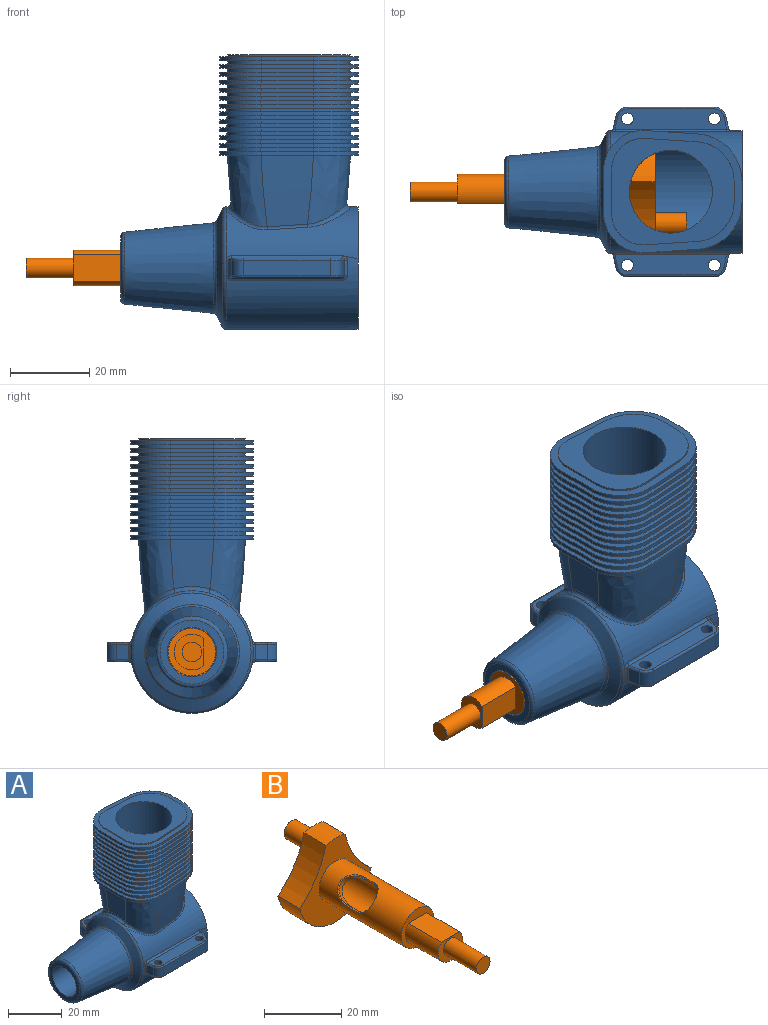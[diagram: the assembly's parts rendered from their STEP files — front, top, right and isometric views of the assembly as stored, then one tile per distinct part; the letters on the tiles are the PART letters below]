
ASSEMBLY  parts=2 mates=1
PART A: 325 faces, bbox 60.4x43.8x74.2 mm
  f0: cylinder r=14mm len=30mm, axis (1,0,0), area 2236mm2, adj f1,f239,f252,f317,f318,f321,f322,f323
  f1: cylinder r=10.5mm len=44.1mm, axis (0,0,1), area 2779.1mm2, adj f0,f20,f317,f318,f319,f320,f321,f322
  f2: bspline ~45.01x32.7mm, area 13.2mm2, adj f7,f9,f18,f56
  f3: bspline ~45.01x29.7mm, area 11mm2, adj f6,f7,f18,f56
  f4: bspline ~45.01x32.7mm, area 13.2mm2, adj f6,f8,f18,f56
  f5: bspline ~45.01x25.49mm, area 5.3mm2, adj f8,f9,f18,f56
  f6: bspline ~8.6x8.58mm, area 13mm2, adj f3,f4,f18,f56
  f7: bspline ~8.6x8.58mm, area 13mm2, adj f2,f3,f18,f56
  f8: bspline ~10.03x9.41mm, area 15mm2, adj f4,f5,f18,f56
  f9: bspline ~10.03x9.41mm, area 15mm2, adj f2,f5,f18,f56
  f10: plane 13.13x1mm, normal (0.06,-1,0), area 13.2mm2, adj f11,f17,f18,f19
  f11: cylinder r=12mm len=11.98mm, axis (0,0,1), area 18.1mm2, adj f10,f12,f18,f19
  f12: plane 5.25x1mm, normal (1,0,0), area 5.2mm2, adj f11,f13,f18,f19
  f13: cylinder r=12mm len=11.98mm, axis (0,0,1), area 18.1mm2, adj f12,f14,f18,f19
  f14: plane 13.13x1mm, normal (0.06,1,0), area 13.2mm2, adj f13,f15,f18,f19
  f15: cylinder r=10mm len=10.64mm, axis (0,0,1), area 16.4mm2, adj f14,f16,f18,f19
  f16: plane 10.93x1mm, normal (-1,0,0), area 10.9mm2, adj f15,f17,f18,f19
  f17: cylinder r=10mm len=10.64mm, axis (0,0,1), area 16.4mm2, adj f10,f16,f18,f19
  f18: plane 35.31x31.24mm, normal (0,0,-1), area 208.1mm2, adj f2,f3,f4,f5,f6,f7,f8,f9
  f19: plane 35.31x31.24mm, normal (0,0,1), area 209mm2, adj f10,f11,f12,f13,f14,f15,f16,f17
  f20: plane 31.29x27.22mm, normal (0,0,1), area 390.9mm2, adj f1,f21,f22,f23,f24,f25,f26,f27
  f21: bspline ~9.98x9.36mm, area 7.5mm2, adj f20,f22,f28,f29
  f22: bspline ~45.01x25.49mm, area 2.6mm2, adj f20,f21,f23,f29
  f23: bspline ~9.98x9.36mm, area 7.5mm2, adj f20,f22,f24,f29
  f24: bspline ~45.01x32.7mm, area 6.6mm2, adj f20,f23,f25,f29
  f25: bspline ~8.54x8.52mm, area 6.5mm2, adj f20,f24,f26,f29
  f26: bspline ~45.01x29.7mm, area 5.5mm2, adj f20,f25,f27,f29
  f27: bspline ~8.54x8.52mm, area 6.5mm2, adj f20,f26,f28,f29
  f28: bspline ~45.01x32.7mm, area 6.6mm2, adj f20,f21,f27,f29
  f29: plane 35.3x31.24mm, normal (0,0,1), area 210.1mm2, adj f21,f22,f23,f24,f25,f26,f27,f28
  f30: cylinder r=12mm len=11.98mm, axis (0,0,1), area 18.1mm2, adj f29,f31,f37,f38
  f31: plane 5.25x1mm, normal (1,0,0), area 5.2mm2, adj f29,f30,f32,f38
  f32: cylinder r=12mm len=11.98mm, axis (0,0,1), area 18.1mm2, adj f29,f31,f33,f38
  f33: plane 13.13x1mm, normal (0.06,1,0), area 13.2mm2, adj f29,f32,f34,f38
  f34: cylinder r=10mm len=10.64mm, axis (0,0,1), area 16.4mm2, adj f29,f33,f35,f38
  f35: plane 10.93x1mm, normal (-1,0,0), area 10.9mm2, adj f29,f34,f36,f38
  f36: cylinder r=10mm len=10.64mm, axis (0,0,1), area 16.4mm2, adj f29,f35,f37,f38
  f37: plane 13.13x1mm, normal (0.06,-1,0), area 13.2mm2, adj f29,f30,f36,f38
  f38: plane 35.31x31.24mm, normal (0,0,-1), area 209.7mm2, adj f30,f31,f32,f33,f34,f35,f36,f37
  f39: bspline ~8.55x8.54mm, area 13mm2, adj f19,f38,f45,f46
  f40: bspline ~8.55x8.54mm, area 13mm2, adj f19,f38,f44,f45
  f41: bspline ~9.99x9.37mm, area 15mm2, adj f19,f38,f43,f44
  f42: bspline ~9.99x9.37mm, area 15mm2, adj f19,f38,f43,f46
  f43: bspline ~45.01x25.49mm, area 5.3mm2, adj f19,f38,f41,f42
  f44: bspline ~45.01x32.7mm, area 13.2mm2, adj f19,f38,f40,f41
  f45: bspline ~45.01x29.7mm, area 10.9mm2, adj f19,f38,f39,f40
  f46: bspline ~45.01x32.7mm, area 13.2mm2, adj f19,f38,f39,f42
  f47: plane 13.13x1mm, normal (0.06,-1,0), area 13.2mm2, adj f48,f54,f55,f56
  f48: cylinder r=12mm len=11.98mm, axis (0,0,1), area 18.1mm2, adj f47,f49,f55,f56
  f49: plane 5.25x1mm, normal (1,0,0), area 5.2mm2, adj f48,f50,f55,f56
  f50: cylinder r=12mm len=11.98mm, axis (0,0,1), area 18.1mm2, adj f49,f51,f55,f56
  f51: plane 13.13x1mm, normal (0.06,1,0), area 13.2mm2, adj f50,f52,f55,f56
  f52: cylinder r=10mm len=10.64mm, axis (0,0,1), area 16.4mm2, adj f51,f53,f55,f56
  f53: plane 10.93x1mm, normal (-1,0,0), area 10.9mm2, adj f52,f54,f55,f56
  f54: cylinder r=10mm len=10.64mm, axis (0,0,1), area 16.4mm2, adj f47,f53,f55,f56
  f55: plane 35.31x31.25mm, normal (0,0,-1), area 205.5mm2, adj f47,f48,f49,f50,f51,f52,f53,f54
  f56: plane 35.31x31.24mm, normal (0,0,1), area 206.9mm2, adj f2,f3,f4,f5,f6,f7,f8,f9
  f57: bspline ~8.6x8.58mm, area 13mm2, adj f55,f63,f64,f74
  f58: bspline ~8.6x8.58mm, area 13mm2, adj f55,f62,f63,f74
  f59: bspline ~10.06x9.45mm, area 15mm2, adj f55,f61,f62,f74
  f60: bspline ~10.06x9.45mm, area 15mm2, adj f55,f61,f64,f74
  f61: bspline ~45.01x25.49mm, area 5.3mm2, adj f55,f59,f60,f74
  f62: bspline ~45.01x32.7mm, area 13.3mm2, adj f55,f58,f59,f74
  f63: bspline ~45.01x29.7mm, area 11mm2, adj f55,f57,f58,f74
  f64: bspline ~45.01x32.7mm, area 13.3mm2, adj f55,f57,f60,f74
  f65: plane 13.13x1mm, normal (0.06,-1,0), area 13.2mm2, adj f66,f72,f73,f74
  f66: cylinder r=12mm len=11.98mm, axis (0,0,1), area 18.1mm2, adj f65,f67,f73,f74
  f67: plane 5.25x1mm, normal (1,0,0), area 5.2mm2, adj f66,f68,f73,f74
  f68: cylinder r=12mm len=11.98mm, axis (0,0,1), area 18.1mm2, adj f67,f69,f73,f74
  f69: plane 13.13x1mm, normal (0.06,1,0), area 13.2mm2, adj f68,f70,f73,f74
  f70: cylinder r=10mm len=10.64mm, axis (0,0,1), area 16.4mm2, adj f69,f71,f73,f74
  f71: plane 10.93x1mm, normal (-1,0,0), area 10.9mm2, adj f70,f72,f73,f74
  f72: cylinder r=10mm len=10.64mm, axis (0,0,1), area 16.4mm2, adj f65,f71,f73,f74
  f73: plane 35.31x31.25mm, normal (0,0,-1), area 202.3mm2, adj f65,f66,f67,f68,f69,f70,f71,f72
  f74: plane 35.31x31.25mm, normal (0,0,1), area 203.9mm2, adj f57,f58,f59,f60,f61,f62,f63,f64
  f75: bspline ~45.01x29.7mm, area 11.1mm2, adj f73,f81,f82,f92
  f76: bspline ~45.01x32.7mm, area 13.3mm2, adj f73,f80,f81,f92
  f77: bspline ~45.01x25.49mm, area 5.4mm2, adj f73,f79,f80,f92
  f78: bspline ~45.01x32.7mm, area 13.3mm2, adj f73,f79,f82,f92
  f79: bspline ~10.04x9.43mm, area 15.1mm2, adj f73,f77,f78,f92
  f80: bspline ~10.04x9.43mm, area 15.1mm2, adj f73,f76,f77,f92
  f81: bspline ~8.63x8.61mm, area 13.1mm2, adj f73,f75,f76,f92
  f82: bspline ~8.63x8.61mm, area 13.1mm2, adj f73,f75,f78,f92
  f83: plane 13.13x1mm, normal (0.06,-1,0), area 13.2mm2, adj f84,f90,f91,f92
  f84: cylinder r=12mm len=11.98mm, axis (0,0,1), area 18.1mm2, adj f83,f85,f91,f92
  f85: plane 5.25x1mm, normal (1,0,0), area 5.2mm2, adj f84,f86,f91,f92
  f86: cylinder r=12mm len=11.98mm, axis (0,0,1), area 18.1mm2, adj f85,f87,f91,f92
  f87: plane 13.13x1mm, normal (0.06,1,0), area 13.2mm2, adj f86,f88,f91,f92
  f88: cylinder r=10mm len=10.64mm, axis (0,0,1), area 16.4mm2, adj f87,f89,f91,f92
  f89: plane 10.93x1mm, normal (-1,0,0), area 10.9mm2, adj f88,f90,f91,f92
  f90: cylinder r=10mm len=10.64mm, axis (0,0,1), area 16.4mm2, adj f83,f89,f91,f92
  f91: plane 35.31x31.25mm, normal (0,0,-1), area 198.8mm2, adj f83,f84,f85,f86,f87,f88,f89,f90
  f92: plane 35.31x31.25mm, normal (0,0,1), area 200.6mm2, adj f75,f76,f77,f78,f79,f80,f81,f82
  f93: bspline ~8.63x8.61mm, area 13.1mm2, adj f91,f99,f100,f110
  f94: bspline ~10.05x9.44mm, area 15.1mm2, adj f91,f98,f99,f110
  f95: bspline ~10.05x9.44mm, area 15.1mm2, adj f91,f97,f98,f110
  f96: bspline ~8.63x8.61mm, area 13.1mm2, adj f91,f97,f100,f110
  f97: bspline ~45.01x32.7mm, area 13.4mm2, adj f91,f95,f96,f110
  f98: bspline ~45.01x25.49mm, area 5.4mm2, adj f91,f94,f95,f110
  f99: bspline ~45.01x32.7mm, area 13.4mm2, adj f91,f93,f94,f110
  f100: bspline ~45.01x29.7mm, area 11.2mm2, adj f91,f93,f96,f110
  f101: plane 13.13x1mm, normal (0.06,-1,0), area 13.2mm2, adj f102,f108,f109,f110
  f102: cylinder r=12mm len=11.98mm, axis (0,0,1), area 18.1mm2, adj f101,f103,f109,f110
  f103: plane 5.25x1mm, normal (1,0,0), area 5.2mm2, adj f102,f104,f109,f110
  f104: cylinder r=12mm len=11.98mm, axis (0,0,1), area 18.1mm2, adj f103,f105,f109,f110
  f105: plane 13.13x1mm, normal (0.06,1,0), area 13.2mm2, adj f104,f106,f109,f110
  f106: cylinder r=10mm len=10.64mm, axis (0,0,1), area 16.4mm2, adj f105,f107,f109,f110
  f107: plane 10.93x1mm, normal (-1,0,0), area 10.9mm2, adj f106,f108,f109,f110
  f108: cylinder r=10mm len=10.64mm, axis (0,0,1), area 16.4mm2, adj f101,f107,f109,f110
  f109: plane 35.31x31.25mm, normal (0,0,-1), area 195.4mm2, adj f101,f102,f103,f104,f105,f106,f107,f108
  f110: plane 35.31x31.25mm, normal (0,0,1), area 197.1mm2, adj f93,f94,f95,f96,f97,f98,f99,f100
  f111: bspline ~45.01x32.7mm, area 13.4mm2, adj f109,f117,f118,f128
  f112: bspline ~45.01x25.49mm, area 5.5mm2, adj f109,f116,f117,f128
  f113: bspline ~45.01x32.7mm, area 13.4mm2, adj f109,f115,f116,f128
  f114: bspline ~45.01x29.7mm, area 11.2mm2, adj f109,f115,f118,f128
  f115: bspline ~8.62x8.6mm, area 13.1mm2, adj f109,f113,f114,f128
  f116: bspline ~10.05x9.44mm, area 15.1mm2, adj f109,f112,f113,f128
  f117: bspline ~10.05x9.44mm, area 15.1mm2, adj f109,f111,f112,f128
  f118: bspline ~8.62x8.6mm, area 13.1mm2, adj f109,f111,f114,f128
  f119: plane 13.13x1mm, normal (0.06,-1,0), area 13.2mm2, adj f120,f126,f127,f128
  f120: cylinder r=12mm len=11.98mm, axis (0,0,1), area 18.1mm2, adj f119,f121,f127,f128
  f121: plane 5.25x1mm, normal (1,0,0), area 5.2mm2, adj f120,f122,f127,f128
  f122: cylinder r=12mm len=11.98mm, axis (0,0,1), area 18.1mm2, adj f121,f123,f127,f128
  f123: plane 13.13x1mm, normal (0.06,1,0), area 13.2mm2, adj f122,f124,f127,f128
  f124: cylinder r=10mm len=10.64mm, axis (0,0,1), area 16.4mm2, adj f123,f125,f127,f128
  f125: plane 10.93x1mm, normal (-1,0,0), area 10.9mm2, adj f124,f126,f127,f128
  f126: cylinder r=10mm len=10.64mm, axis (0,0,1), area 16.4mm2, adj f119,f125,f127,f128
  f127: plane 35.31x31.24mm, normal (0,0,-1), area 192.5mm2, adj f119,f120,f121,f122,f123,f124,f125,f126
  f128: plane 35.31x31.25mm, normal (0,0,1), area 193.9mm2, adj f111,f112,f113,f114,f115,f116,f117,f118
  f129: bspline ~10.03x9.41mm, area 15.1mm2, adj f127,f135,f136,f146
  f130: bspline ~10.03x9.41mm, area 15.1mm2, adj f127,f134,f135,f146
  f131: bspline ~10.73x8.62mm, area 13.1mm2, adj f127,f133,f134,f146
  f132: bspline ~10.73x8.62mm, area 13.1mm2, adj f127,f133,f136,f146
  f133: bspline ~45.01x29.7mm, area 11.3mm2, adj f127,f131,f132,f146
  f134: bspline ~45.01x32.7mm, area 13.5mm2, adj f127,f130,f131,f146
  f135: bspline ~45.01x25.49mm, area 5.5mm2, adj f127,f129,f130,f146
  f136: bspline ~45.01x32.7mm, area 13.5mm2, adj f127,f129,f132,f146
  f137: plane 13.13x1mm, normal (0.06,-1,0), area 13.2mm2, adj f138,f144,f145,f146
  f138: cylinder r=12mm len=11.98mm, axis (0,0,1), area 18.1mm2, adj f137,f139,f145,f146
  f139: plane 5.25x1mm, normal (1,0,0), area 5.2mm2, adj f138,f140,f145,f146
  f140: cylinder r=12mm len=11.98mm, axis (0,0,1), area 18.1mm2, adj f139,f141,f145,f146
  f141: plane 13.13x1mm, normal (0.06,1,0), area 13.2mm2, adj f140,f142,f145,f146
  f142: cylinder r=10mm len=10.64mm, axis (0,0,1), area 16.4mm2, adj f141,f143,f145,f146
  f143: plane 10.93x1mm, normal (-1,0,0), area 10.9mm2, adj f142,f144,f145,f146
  f144: cylinder r=10mm len=10.64mm, axis (0,0,1), area 16.4mm2, adj f137,f143,f145,f146
  f145: plane 35.31x31.24mm, normal (0,0,-1), area 190.3mm2, adj f137,f138,f139,f140,f141,f142,f143,f144
  f146: plane 35.31x31.24mm, normal (0,0,1), area 191.3mm2, adj f129,f130,f131,f132,f133,f134,f135,f136
  f147: bspline ~45.01x25.49mm, area 5.6mm2, adj f145,f153,f154,f164
  f148: bspline ~45.01x32.7mm, area 13.5mm2, adj f145,f152,f153,f164
  f149: bspline ~45.01x29.7mm, area 11.3mm2, adj f145,f151,f152,f164
  f150: bspline ~45.01x32.7mm, area 13.5mm2, adj f145,f151,f154,f164
  f151: bspline ~8.57x8.55mm, area 13.2mm2, adj f145,f149,f150,f164
  f152: bspline ~8.57x8.55mm, area 13.2mm2, adj f145,f148,f149,f164
  f153: bspline ~10.03x9.44mm, area 15.2mm2, adj f145,f147,f148,f164
  f154: bspline ~10.03x9.44mm, area 15.2mm2, adj f145,f147,f150,f164
  f155: plane 13.13x1mm, normal (0.06,-1,0), area 13.2mm2, adj f156,f162,f163,f164
  f156: cylinder r=12mm len=11.98mm, axis (0,0,1), area 18.1mm2, adj f155,f157,f163,f164
  f157: plane 5.25x1mm, normal (1,0,0), area 5.2mm2, adj f156,f158,f163,f164
  f158: cylinder r=12mm len=11.98mm, axis (0,0,1), area 18.1mm2, adj f157,f159,f163,f164
  f159: plane 13.13x1mm, normal (0.06,1,0), area 13.2mm2, adj f158,f160,f163,f164
  f160: cylinder r=10mm len=10.64mm, axis (0,0,1), area 16.4mm2, adj f159,f161,f163,f164
  f161: plane 10.93x1mm, normal (-1,0,0), area 10.9mm2, adj f160,f162,f163,f164
  f162: cylinder r=10mm len=10.64mm, axis (0,0,1), area 16.4mm2, adj f155,f161,f163,f164
  f163: plane 35.3x31.24mm, normal (0,0,-1), area 189.2mm2, adj f155,f156,f157,f158,f159,f160,f161,f162
  f164: plane 35.31x31.24mm, normal (0,0,1), area 189.6mm2, adj f147,f148,f149,f150,f151,f152,f153,f154
  f165: bspline ~9.99x9.37mm, area 15.2mm2, adj f163,f171,f172,f182
  f166: bspline ~11.01x8.6mm, area 13.2mm2, adj f163,f170,f171,f182
  f167: bspline ~11.01x8.6mm, area 13.2mm2, adj f163,f169,f170,f182
  f168: bspline ~9.99x9.37mm, area 15.2mm2, adj f163,f169,f172,f182
  f169: bspline ~45.01x32.7mm, area 13.5mm2, adj f163,f167,f168,f182
  f170: bspline ~45.01x29.7mm, area 11.3mm2, adj f163,f166,f167,f182
  f171: bspline ~45.01x32.7mm, area 13.5mm2, adj f163,f165,f166,f182
  f172: bspline ~45.01x25.49mm, area 5.6mm2, adj f163,f165,f168,f182
  f173: plane 13.13x1mm, normal (0.06,-1,0), area 13.2mm2, adj f174,f180,f181,f182
  f174: cylinder r=12mm len=11.98mm, axis (0,0,1), area 18.1mm2, adj f173,f175,f181,f182
  f175: plane 5.25x1mm, normal (1,0,0), area 5.2mm2, adj f174,f176,f181,f182
  f176: cylinder r=12mm len=11.98mm, axis (0,0,1), area 18.1mm2, adj f175,f177,f181,f182
  f177: plane 13.13x1mm, normal (0.06,1,0), area 13.2mm2, adj f176,f178,f181,f182
  f178: cylinder r=10mm len=10.64mm, axis (0,0,1), area 16.4mm2, adj f177,f179,f181,f182
  f179: plane 10.93x1mm, normal (-1,0,0), area 10.9mm2, adj f178,f180,f181,f182
  f180: cylinder r=10mm len=10.64mm, axis (0,0,1), area 16.4mm2, adj f173,f179,f181,f182
  f181: plane 35.31x31.24mm, normal (0,0,-1), area 189.6mm2, adj f173,f174,f175,f176,f177,f178,f179,f180
  f182: plane 35.3x31.24mm, normal (0,0,1), area 189.2mm2, adj f165,f166,f167,f168,f169,f170,f171,f172
  f183: bspline ~45.01x32.7mm, area 13.5mm2, adj f181,f189,f190,f200
  f184: bspline ~45.01x29.7mm, area 11.3mm2, adj f181,f188,f189,f200
  f185: bspline ~45.01x32.7mm, area 13.5mm2, adj f181,f187,f188,f200
  f186: bspline ~45.01x25.49mm, area 5.6mm2, adj f181,f187,f190,f200
  f187: bspline ~10.05x9.43mm, area 15.2mm2, adj f181,f185,f186,f200
  f188: bspline ~8.6x8.58mm, area 13.2mm2, adj f181,f184,f185,f200
  f189: bspline ~8.6x8.58mm, area 13.2mm2, adj f181,f183,f184,f200
  f190: bspline ~10.05x9.43mm, area 15.2mm2, adj f181,f183,f186,f200
  f191: plane 13.13x1mm, normal (0.06,-1,0), area 13.2mm2, adj f192,f198,f199,f200
  f192: cylinder r=12mm len=11.98mm, axis (0,0,1), area 18.1mm2, adj f191,f193,f199,f200
  f193: plane 5.25x1mm, normal (1,0,0), area 5.2mm2, adj f192,f194,f199,f200
  f194: cylinder r=12mm len=11.98mm, axis (0,0,1), area 18.1mm2, adj f193,f195,f199,f200
  f195: plane 13.13x1mm, normal (0.06,1,0), area 13.2mm2, adj f194,f196,f199,f200
  f196: cylinder r=10mm len=10.64mm, axis (0,0,1), area 16.4mm2, adj f195,f197,f199,f200
  f197: plane 10.93x1mm, normal (-1,0,0), area 10.9mm2, adj f196,f198,f199,f200
  f198: cylinder r=10mm len=10.64mm, axis (0,0,1), area 16.4mm2, adj f191,f197,f199,f200
  f199: plane 35.31x31.25mm, normal (0,0,-1), area 191.8mm2, adj f191,f192,f193,f194,f195,f196,f197,f198
  f200: plane 35.31x31.24mm, normal (0,0,1), area 190.5mm2, adj f183,f184,f185,f186,f187,f188,f189,f190
  f201: bspline ~12.75x8.81mm, area 13.2mm2, adj f199,f207,f208,f218
  f202: bspline ~12.75x8.81mm, area 13.2mm2, adj f199,f206,f207,f218
  f203: bspline ~10.05x9.43mm, area 15.2mm2, adj f199,f205,f206,f218
  f204: bspline ~10.05x9.43mm, area 15.2mm2, adj f199,f205,f208,f218
  f205: bspline ~45.01x25.49mm, area 5.5mm2, adj f199,f203,f204,f218
  f206: bspline ~45.01x32.7mm, area 13.5mm2, adj f199,f202,f203,f218
  f207: bspline ~45.01x29.7mm, area 11.3mm2, adj f199,f201,f202,f218
  f208: bspline ~45.01x32.7mm, area 13.5mm2, adj f199,f201,f204,f218
  f209: plane 13.13x1mm, normal (0.06,-1,0), area 13.2mm2, adj f210,f216,f217,f218
  f210: cylinder r=12mm len=11.98mm, axis (0,0,1), area 18.1mm2, adj f209,f211,f217,f218
  f211: plane 5.25x1mm, normal (1,0,0), area 5.2mm2, adj f210,f212,f217,f218
  f212: cylinder r=12mm len=11.98mm, axis (0,0,1), area 18.1mm2, adj f211,f213,f217,f218
  f213: plane 13.13x1mm, normal (0.06,1,0), area 13.2mm2, adj f212,f214,f217,f218
  f214: cylinder r=10mm len=10.64mm, axis (0,0,1), area 16.4mm2, adj f213,f215,f217,f218
  f215: plane 10.93x1mm, normal (-1,0,0), area 10.9mm2, adj f214,f216,f217,f218
  f216: cylinder r=10mm len=10.64mm, axis (0,0,1), area 16.4mm2, adj f209,f215,f217,f218
  f217: plane 35.33x31.26mm, normal (0,0,-1), area 196.2mm2, adj f209,f210,f211,f212,f213,f214,f215,f216
  f218: plane 35.32x31.25mm, normal (0,0,1), area 193.7mm2, adj f201,f202,f203,f204,f205,f206,f207,f208
  f219: bspline ~45.01x29.7mm, area 11.2mm2, adj f217,f225,f226,f236
  f220: bspline ~45.01x32.7mm, area 13.4mm2, adj f217,f224,f225,f236
  f221: bspline ~45.01x25.49mm, area 5.5mm2, adj f217,f223,f224,f236
  f222: bspline ~45.01x32.7mm, area 13.4mm2, adj f217,f223,f226,f236
  f223: bspline ~10.16x9.57mm, area 15.3mm2, adj f217,f221,f222,f236
  f224: bspline ~10.16x9.57mm, area 15.3mm2, adj f217,f220,f221,f236
  f225: bspline ~8.79x8.78mm, area 13.3mm2, adj f217,f219,f220,f236
  f226: bspline ~8.79x8.78mm, area 13.3mm2, adj f217,f219,f222,f236
  f227: plane 13.13x1mm, normal (0.06,-1,0), area 13.2mm2, adj f228,f234,f235,f236
  f228: cylinder r=12mm len=11.98mm, axis (0,0,1), area 18.1mm2, adj f227,f229,f235,f236
  f229: plane 5.25x1mm, normal (1,0,0), area 5.2mm2, adj f228,f230,f235,f236
  f230: cylinder r=12mm len=11.98mm, axis (0,0,1), area 18.1mm2, adj f229,f231,f235,f236
  f231: plane 13.13x1mm, normal (0.06,1,0), area 13.2mm2, adj f230,f232,f235,f236
  f232: cylinder r=10mm len=10.64mm, axis (0,0,1), area 16.4mm2, adj f231,f233,f235,f236
  f233: plane 10.93x1mm, normal (-1,0,0), area 10.9mm2, adj f232,f234,f235,f236
  f234: cylinder r=10mm len=10.64mm, axis (0,0,1), area 16.4mm2, adj f227,f233,f235,f236
  f235: plane 35.35x31.29mm, normal (0,0,-1), area 203mm2, adj f227,f228,f229,f230,f231,f232,f233,f234
  f236: plane 35.34x31.27mm, normal (0,0,1), area 199.3mm2, adj f219,f220,f221,f222,f223,f224,f225,f226
  f237: cylinder r=6.25mm len=30mm, axis (-1,0,0), area 1178.1mm2, adj f238,f239
  f238: plane 16.2x16.2mm, normal (-1,0,0), area 83.4mm2, adj f237,f316
  f239: plane 28x28mm, normal (1,0,0), area 493mm2, adj f0,f237
  f240: cone r=9mm half-angle=6deg, axis (1,0,0), area 1465.2mm2, adj f315,f316
  f241: cylinder r=3mm len=4mm, axis (0,0,-1), area 16.3mm2, adj f242,f254,f273,f283
  f242: plane 22x4mm, normal (0,1,0), area 88mm2, adj f241,f245,f272,f282
  f243: cylinder r=1.5mm len=5mm, axis (0,0,1), area 47.1mm2, adj f253,f255
  f244: cylinder r=1.5mm len=5mm, axis (0,0,1), area 47.1mm2, adj f253,f255
  f245: cylinder r=3mm len=4mm, axis (0,0,-1), area 16.3mm2, adj f242,f256,f271,f281
  f246: cylinder r=3mm len=4mm, axis (0,0,-1), area 16.3mm2, adj f247,f258,f276,f286
  f247: plane 22x4mm, normal (0,-1,0), area 88mm2, adj f246,f250,f277,f287
  f248: cylinder r=1.5mm len=5mm, axis (0,0,1), area 47.1mm2, adj f257,f259
  f249: cylinder r=1.5mm len=5mm, axis (0,0,1), area 47.1mm2, adj f257,f259
  f250: cylinder r=3mm len=4mm, axis (0,0,-1), area 16.3mm2, adj f247,f260,f278,f288
  f251: cone r=11.52mm half-angle=63.3deg, axis (1,0,0), area 278.6mm2, adj f314,f315
  f252: plane 31x31mm, normal (1,0,0), area 139mm2, adj f0,f261
  f253: plane 28.21x5.08mm, normal (0,0,-1), area 122mm2, adj f243,f244,f270,f271,f272,f273,f274,f305
  f254: plane 4x3.15mm, normal (-0.98,0.21,0), area 12.6mm2, adj f241,f274,f284,f302
  f255: plane 28.21x5.08mm, normal (0,0,1), area 122mm2, adj f243,f244,f280,f281,f282,f283,f284,f298
  f256: plane 4x3.15mm, normal (0.98,0.21,0), area 12.6mm2, adj f245,f270,f280,f301
  f257: plane 28.21x5.08mm, normal (0,0,-1), area 122mm2, adj f248,f249,f275,f276,f277,f278,f279,f297
  f258: plane 4x3.15mm, normal (0.98,-0.21,0), area 12.6mm2, adj f246,f275,f285,f294
  f259: plane 28.21x5.08mm, normal (0,0,1), area 122mm2, adj f248,f249,f285,f286,f287,f288,f289,f290
  f260: plane 4x3.15mm, normal (-0.98,-0.21,0), area 12.6mm2, adj f250,f279,f289,f293
  f261: cylinder r=15.5mm len=33.38mm, axis (1,0,0), area 2139.1mm2, adj f252,f290,f291,f292,f293,f294,f295,f296
  f262: bspline ~27.82x10.76mm, area 203.5mm2, adj f235,f268,f269,f306
  f263: bspline ~27.67x11.96mm, area 224.8mm2, adj f235,f267,f268,f310
  f264: bspline ~27.67x11.96mm, area 224.8mm2, adj f235,f266,f267,f313
  f265: bspline ~27.82x10.76mm, area 203.5mm2, adj f235,f266,f269,f309
  f266: bspline ~54x32.7mm, area 210.8mm2, adj f235,f264,f265,f311
  f267: bspline ~54x25.49mm, area 55.9mm2, adj f235,f263,f264,f312
  f268: bspline ~54x32.7mm, area 210.8mm2, adj f235,f262,f263,f308
  f269: bspline ~54x29.7mm, area 128.4mm2, adj f235,f262,f265,f307
  f270: cylinder r=0.5mm len=3.26mm, axis (-0.21,0.98,0), area 2.5mm2, adj f253,f256,f271,f303
  f271: torus R=2.5mm, axis (0,0,1), area 3mm2, adj f245,f253,f270,f272
  f272: cylinder r=0.5mm len=22mm, axis (-1,0,0), area 17.3mm2, adj f242,f253,f271,f273
  f273: torus R=2.5mm, axis (0,0,1), area 3mm2, adj f241,f253,f272,f274
  f274: cylinder r=0.5mm len=3.26mm, axis (-0.21,-0.98,0), area 2.5mm2, adj f253,f254,f273,f304
  f275: cylinder r=0.5mm len=3.26mm, axis (0.21,0.98,0), area 2.5mm2, adj f257,f258,f276,f296
  f276: torus R=2.5mm, axis (0,0,1), area 3mm2, adj f246,f257,f275,f277
  f277: cylinder r=0.5mm len=22mm, axis (1,0,0), area 17.3mm2, adj f247,f257,f276,f278
  f278: torus R=2.5mm, axis (0,0,1), area 3mm2, adj f250,f257,f277,f279
  f279: cylinder r=0.5mm len=3.26mm, axis (0.21,-0.98,0), area 2.5mm2, adj f257,f260,f278,f295
  f280: cylinder r=0.5mm len=3.26mm, axis (0.21,-0.98,0), area 2.5mm2, adj f255,f256,f281,f299
  f281: torus R=2.5mm, axis (0,0,1), area 3mm2, adj f245,f255,f280,f282
  f282: cylinder r=0.5mm len=22mm, axis (1,0,0), area 17.3mm2, adj f242,f255,f281,f283
  f283: torus R=2.5mm, axis (0,0,1), area 3mm2, adj f241,f255,f282,f284
  f284: cylinder r=0.5mm len=3.26mm, axis (0.21,0.98,0), area 2.5mm2, adj f254,f255,f283,f300
  f285: cylinder r=0.5mm len=3.26mm, axis (-0.21,-0.98,0), area 2.5mm2, adj f258,f259,f286,f292
  f286: torus R=2.5mm, axis (0,0,1), area 3mm2, adj f246,f259,f285,f287
  f287: cylinder r=0.5mm len=22mm, axis (-1,0,0), area 17.3mm2, adj f247,f259,f286,f288
  f288: torus R=2.5mm, axis (0,0,1), area 3mm2, adj f250,f259,f287,f289
  f289: cylinder r=0.5mm len=3.26mm, axis (-0.21,0.98,0), area 2.5mm2, adj f259,f260,f288,f291
  f290: cylinder r=0.75mm len=28.21mm, axis (1,0,0), area 29mm2, adj f259,f261,f291,f292
  f291: bspline ~1.53x1.46mm, area 1.2mm2, adj f261,f289,f290,f293
  f292: bspline ~1.53x1.46mm, area 1.2mm2, adj f261,f285,f290,f294
  f293: bspline ~4x0.76mm, area 4mm2, adj f260,f261,f291,f295
  f294: bspline ~4x0.76mm, area 4mm2, adj f258,f261,f292,f296
  f295: bspline ~1.53x1.46mm, area 1.2mm2, adj f261,f279,f293,f297
  f296: bspline ~1.53x1.46mm, area 1.2mm2, adj f261,f275,f294,f297
  f297: cylinder r=0.75mm len=28.21mm, axis (1,0,0), area 29mm2, adj f257,f261,f295,f296
  f298: cylinder r=0.75mm len=28.21mm, axis (1,0,0), area 29mm2, adj f255,f261,f299,f300
  f299: bspline ~1.53x1.46mm, area 1.2mm2, adj f261,f280,f298,f301
  f300: bspline ~1.53x1.46mm, area 1.2mm2, adj f261,f284,f298,f302
  f301: bspline ~4x0.76mm, area 4mm2, adj f256,f261,f299,f303
  f302: bspline ~4x0.76mm, area 4mm2, adj f254,f261,f300,f304
  f303: bspline ~1.53x1.46mm, area 1.2mm2, adj f261,f270,f301,f305
  f304: bspline ~1.53x1.46mm, area 1.2mm2, adj f261,f274,f302,f305
  f305: cylinder r=0.75mm len=28.21mm, axis (1,0,0), area 29mm2, adj f253,f261,f303,f304
  f306: bspline ~11.84x9.37mm, area 17.8mm2, adj f261,f262,f307,f308
  f307: bspline ~12.74x2.31mm, area 15.1mm2, adj f261,f269,f306,f309
  f308: bspline ~21.25x2.14mm, area 8.4mm2, adj f261,f268,f306,f310
  f309: bspline ~10.62x9.37mm, area 17.8mm2, adj f261,f265,f307,f311
  f310: bspline ~11.73x11.38mm, area 21mm2, adj f261,f263,f308,f312
  f311: bspline ~21.25x2.14mm, area 8.4mm2, adj f261,f266,f309,f313
  f312: bspline ~7.54x1.51mm, area 6.3mm2, adj f261,f267,f310,f313
  f313: bspline ~12.84x11.73mm, area 21mm2, adj f261,f264,f311,f312
  f314: torus R=14.5mm, axis (-1,0,0), area 106.3mm2, adj f251,f261
  f315: torus R=12.46mm, axis (1,0,0), area 73.3mm2, adj f240,f251
  f316: torus R=8.1mm, axis (1,0,0), area 80.2mm2, adj f238,f240
  f317: plane 3.69x1.52mm, normal (-1,0,0), area 1.2mm2, adj f0,f1,f319,f323
  f318: plane 3.69x1.52mm, normal (1,0,0), area 1.2mm2, adj f0,f1,f319,f323
  f319: cylinder r=11mm len=7mm, axis (1,0,0), area 7.9mm2, adj f1,f317,f318,f323
  f320: cylinder r=11mm len=7mm, axis (1,0,0), area 7.9mm2, adj f1,f321,f322,f324
  f321: plane 3.69x1.52mm, normal (1,0,0), area 1.2mm2, adj f0,f1,f320,f324
  f322: plane 3.69x1.52mm, normal (-1,0,0), area 1.2mm2, adj f0,f1,f320,f324
  f323: cylinder r=5mm len=7mm, axis (1,0,0), area 12.8mm2, adj f0,f317,f318,f319
  f324: cylinder r=5mm len=7mm, axis (-1,0,0), area 12.8mm2, adj f0,f320,f321,f322
PART B: 25 faces, bbox 26x70x26.5 mm
  f0: cylinder r=6mm len=30mm, axis (0,1,0), area 1028.4mm2, adj f5,f17,f21,f22,f23,f24
  f1: cylinder r=28mm len=15.34mm, axis (0,1,0), area 147mm2, adj f2,f4,f5,f6
  f2: cylinder r=13.25mm len=8mm, axis (0,1,0), area 56.7mm2, adj f1,f3,f5,f6
  f3: cylinder r=28mm len=15.34mm, axis (0,1,0), area 147mm2, adj f2,f4,f5,f6
  f4: cylinder r=13.25mm len=26mm, axis (0,1,0), area 291.8mm2, adj f1,f3,f5,f6
  f5: plane 26.5x26mm, normal (0,-1,0), area 314.4mm2, adj f0,f1,f2,f3,f4
  f6: plane 26.5x26mm, normal (0,1,0), area 347mm2, adj f1,f2,f3,f4,f7,f9
  f7: cylinder r=2.75mm len=8mm, axis (0,-1,0), area 138.2mm2, adj f6,f8
  f8: plane 5.5x5.5mm, normal (0,1,0), area 23.8mm2, adj f7
  f9: cylinder r=4.25mm len=27mm, axis (0,1,0), area 620.8mm2, adj f6,f10,f11,f12,f13,f14
  f10: plane 8.5x8.5mm, normal (0,1,0), area 56.7mm2, adj f9
  f11: plane 4x1.77mm, normal (-0.71,0,-0.71), area 10mm2, adj f9,f12,f14,f22
  f12: cylinder r=4mm len=8.73mm, axis (0.71,0,-0.71), area 23.2mm2, adj f9,f11,f13,f21
  f13: plane 4x1.77mm, normal (0.71,0,0.71), area 10mm2, adj f9,f12,f14,f23
  f14: cylinder r=4mm len=8.73mm, axis (0.71,0,-0.71), area 23.2mm2, adj f9,f11,f13,f24
  f15: cylinder r=4.5mm len=12mm, axis (0,-1,0), area 248.5mm2, adj f16,f17,f19
  f16: plane 12x6.71mm, normal (0,0,1), area 80.5mm2, adj f15,f17,f19
  f17: plane 12x12mm, normal (0,-1,0), area 56.4mm2, adj f0,f15,f16
  f18: cylinder r=2.5mm len=12mm, axis (0,-1,0), area 188.5mm2, adj f19,f20
  f19: plane 9x7.5mm, normal (0,-1,0), area 37mm2, adj f15,f16,f18
  f20: plane 5x5mm, normal (0,-1,0), area 19.6mm2, adj f18
  f21: bspline ~6.22x6.22mm, area 5mm2, adj f0,f12,f22,f23
  f22: plane 4x0.38mm, normal (-0.92,0,0.4), area 1.7mm2, adj f0,f11,f21,f24
  f23: plane 4x0.38mm, normal (-0.4,0,0.92), area 1.7mm2, adj f0,f13,f21,f24
  f24: bspline ~6.22x6.22mm, area 5mm2, adj f0,f14,f22,f23
PLACE A at identity
PLACE B rot(axis=(0.58,0.58,-0.58),120deg) t=(38,0,0)mm
MATE revolute B.f4 <-> A.f0  axis (-1,0,0) through (30,0,0)mm
